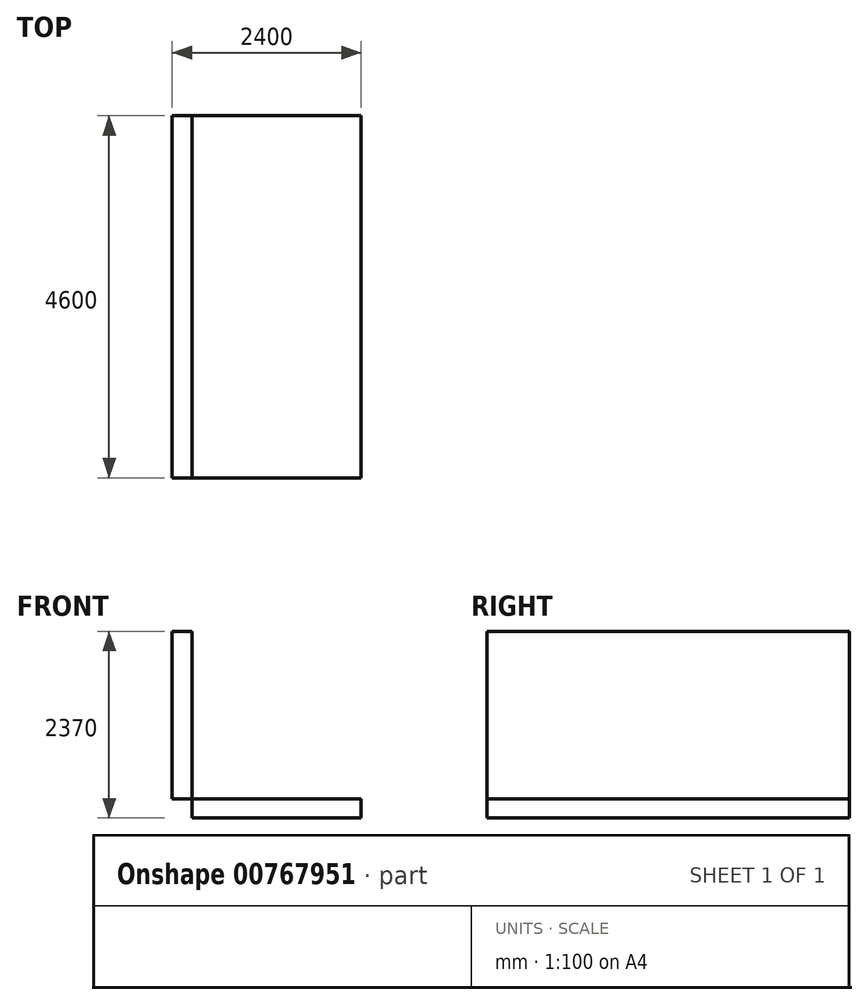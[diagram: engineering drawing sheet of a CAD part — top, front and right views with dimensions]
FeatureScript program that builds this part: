
annotation { "Feature Type Name" : "Feature", "Feature Type Description" : "" }
export const myFeature = defineFeature(function(context is Context, id is Id, definition is map)
    precondition{}
    {
        {
            var Q0;
            Q0=qCreatedBy(makeId("Front.planeOp"),FACE);
            var sketch = newSketch(context, id + "F0", { "sketchPlane" : qUnion([Q0])});
            skLineSegment(sketch, "E0.bottom", {"start": v(0, 0) * mm, "end": v(1000, 0) * mm});
            skLineSegment(sketch, "E0.top", {"start": v(0, 1030) * mm, "end": v(1000, 1030) * mm});
            skLineSegment(sketch, "E0.left", {"start": v(0, 0) * mm, "end": v(0, 1030) * mm});
            skLineSegment(sketch, "E0.right", {"start": v(1000, 0) * mm, "end": v(1000, 1030) * mm});
            skSolve(sketch);
        }
        {
            var Q0;
            Q0=makeQuery(id+"F0.imprint","IMPRINT",FACE,{"disambiguationData":[TD([[makeQuery(id+"F0.imprint","IMPRINT",EDGE,{"derivedFrom":sQuery(id+"F0.wireOp",EDGE,"E0.bottom")}),1.0]])]});
            extrude(context, id + "F1", {"entities" : qUnion([Q0]), "depth" : 1 * mm, "offsetDistance" : 25 * mm});
        }
        {
            var Q0;
            Q0=qCreatedBy(makeId("Top.planeOp"),FACE);
            var sketch = newSketch(context, id + "F2", { "sketchPlane" : qUnion([Q0])});
            skLineSegment(sketch, "E1.bottom", {"start": v(0, 0) * mm, "end": v(995.1, 0) * mm});
            skLineSegment(sketch, "E1.top", {"start": v(0, -1797.59) * mm, "end": v(995.1, -1797.59) * mm});
            skLineSegment(sketch, "E1.left", {"start": v(0, 0) * mm, "end": v(0, -1797.59) * mm});
            skLineSegment(sketch, "E1.right", {"start": v(995.1, 0) * mm, "end": v(995.1, -1797.59) * mm});
            skSolve(sketch);
        }
        {
            var Q0;
            Q0=makeQuery(id+"F2.imprint","IMPRINT",FACE,{"disambiguationData":[TD([[makeQuery(id+"F2.imprint","IMPRINT",EDGE,{"derivedFrom":sQuery(id+"F2.wireOp",EDGE,"E1.bottom")}),-1.0]])]});
            extrude(context, id + "F3", {"entities" : qUnion([Q0]), "operationType" : NewBodyOperationType.ADD, "depth" : 100 * mm, "offsetDistance" : 25 * mm});
        }
        {
            var Q0;
            Q0=makeQuery(id+"F1.opExtrude","SWEPT_BODY",BODY,{"disambiguationData":[OSD([sQuery(id+"F0.wireOp",EDGE,"E0.bottom"),sQuery(id+"F0.wireOp",EDGE,"E0.top"),sQuery(id+"F0.wireOp",EDGE,"E0.left"),sQuery(id+"F0.wireOp",EDGE,"E0.right")])]});
            deleteBodies(context, id + "F4", {"entities" : qUnion([Q0])});
        }
        {
            var Q0;
            Q0=qCreatedBy(makeId("Top.planeOp"),FACE);
            var sketch = newSketch(context, id + "F5", { "sketchPlane" : qUnion([Q0])});
            skLineSegment(sketch, "E2.bottom", {"start": v(-1969.21, 1837) * mm, "end": v(180.79, 1837) * mm});
            skLineSegment(sketch, "E2.top", {"start": v(-1969.21, -2763) * mm, "end": v(180.79, -2763) * mm});
            skLineSegment(sketch, "E2.left", {"start": v(-1969.21, 1837) * mm, "end": v(-1969.21, -2763) * mm});
            skLineSegment(sketch, "E2.right", {"start": v(180.79, 1837) * mm, "end": v(180.79, -2763) * mm});
            skSolve(sketch);
        }
        {
            var Q0;
            Q0=makeQuery(id+"F5.imprint","IMPRINT",FACE,{"disambiguationData":[TD([[makeQuery(id+"F5.imprint","IMPRINT",EDGE,{"derivedFrom":sQuery(id+"F5.wireOp",EDGE,"E2.bottom")}),-1.0]])]});
            extrude(context, id + "F6", {"entities" : qUnion([Q0]), "depth" : 240 * mm, "offsetDistance" : 25 * mm});
        }
        {
            var Q0;
            Q0=makeQuery(id+"F6.opExtrude","SWEPT_FACE",FACE,{"disambiguationData":[OSD([sQuery(id+"F5.wireOp",EDGE,"E2.left")])]});
            var sketch = newSketch(context, id + "F7", { "sketchPlane" : qUnion([Q0])});
            skLineSegment(sketch, "E3.bottom", {"start": v(2763, 240) * mm, "end": v(-1837, 240) * mm});
            skLineSegment(sketch, "E3.top", {"start": v(2763, 2370) * mm, "end": v(-1837, 2370) * mm});
            skLineSegment(sketch, "E3.left", {"start": v(2763, 240) * mm, "end": v(2763, 2370) * mm});
            skLineSegment(sketch, "E3.right", {"start": v(-1837, 240) * mm, "end": v(-1837, 2370) * mm});
            skSolve(sketch);
        }
        {
            var Q0;
            Q0=makeQuery(id+"F7.imprint","IMPRINT",FACE,{"disambiguationData":[TD([[makeQuery(id+"F7.imprint","IMPRINT",EDGE,{"derivedFrom":sQuery(id+"F7.wireOp",EDGE,"E3.bottom")}),1.0]])]});
            extrude(context, id + "F8", {"entities" : qUnion([Q0]), "depth" : 250 * mm, "offsetDistance" : 25 * mm});
        }
    });
